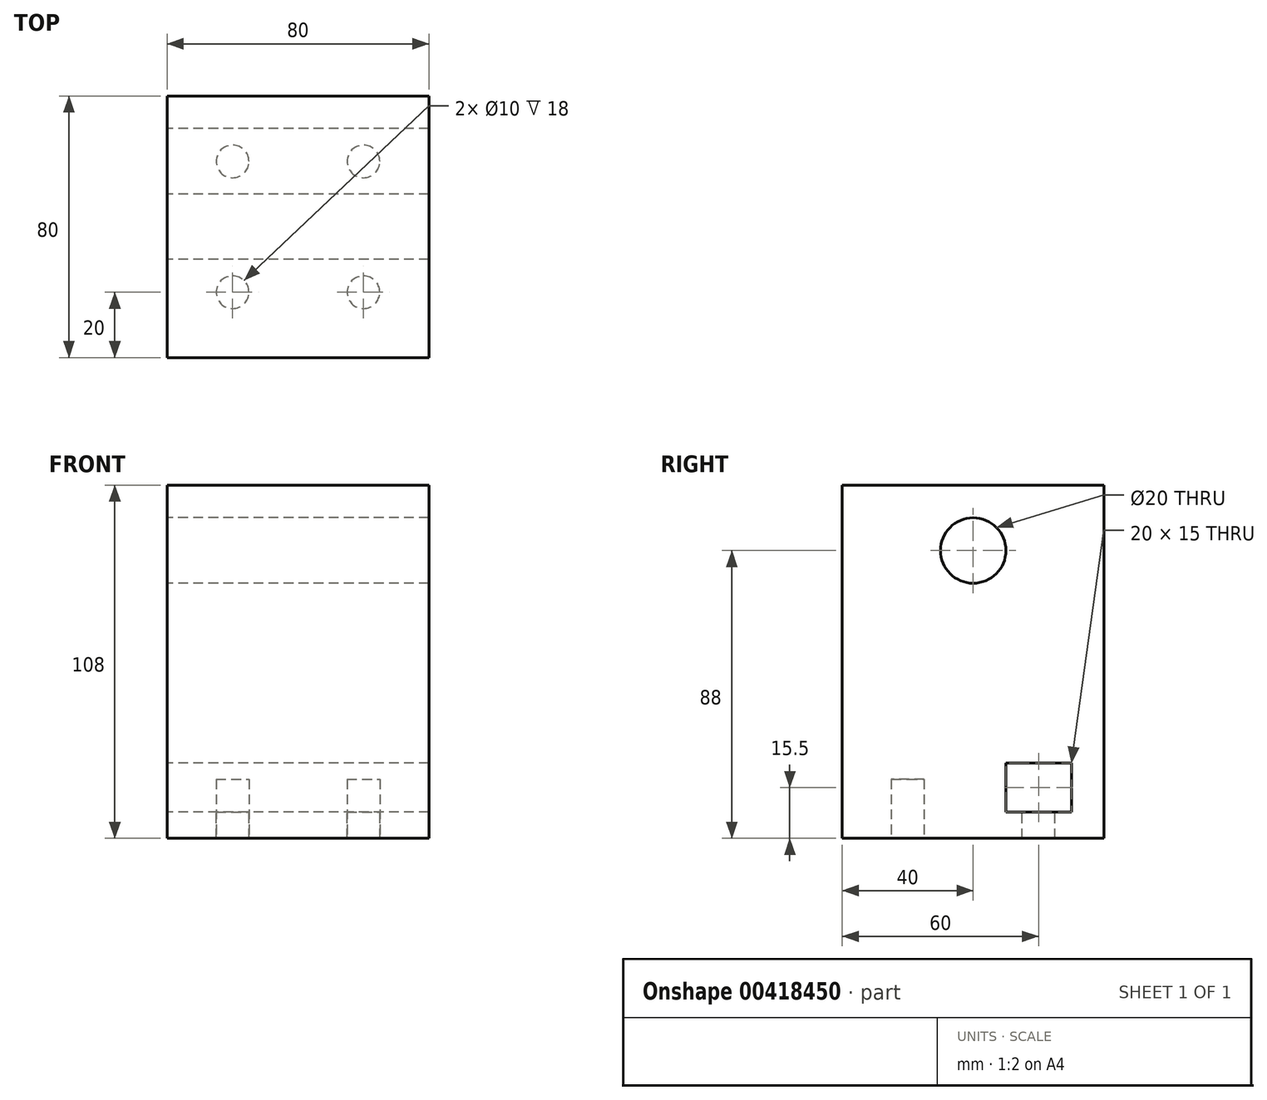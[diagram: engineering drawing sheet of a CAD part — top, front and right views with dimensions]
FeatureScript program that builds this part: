
annotation { "Feature Type Name" : "Feature", "Feature Type Description" : "" }
export const myFeature = defineFeature(function(context is Context, id is Id, definition is map)
    precondition{}
    {
        {
            var Q0;
            Q0=qCreatedBy(makeId("Top.planeOp"),FACE);
            var sketch = newSketch(context, id + "F0", { "sketchPlane" : qUnion([Q0])});
            skLineSegment(sketch, "E0.bottom", {"start": v(40, -40) * mm, "end": v(-40, -40) * mm});
            skLineSegment(sketch, "E0.top", {"start": v(40, 40) * mm, "end": v(-40, 40) * mm});
            skLineSegment(sketch, "E0.left", {"start": v(40, -40) * mm, "end": v(40, 40) * mm});
            skLineSegment(sketch, "E0.right", {"start": v(-40, -40) * mm, "end": v(-40, 40) * mm});
            skPoint(sketch, "E0.middle", {"position": v(0, 0) * mm});
            skSolve(sketch);
        }
        {
            var Q0;
            Q0=makeQuery(id+"F0.imprint","IMPRINT",FACE,{"disambiguationData":[TD([[makeQuery(id+"F0.imprint","IMPRINT",EDGE,{"derivedFrom":sQuery(id+"F0.wireOp",EDGE,"E0.bottom")}),-1.0]])]});
            extrude(context, id + "F1", {"entities" : qUnion([Q0]), "endBound" : BoundingType.SYMMETRIC, "depth" : 100 * mm});
        }
        {
            var Q0;
            Q0=makeQuery(id+"F1.opExtrude","CAP_FACE",FACE,{"disambiguationData":[OSD([sQuery(id+"F0.wireOp",EDGE,"E0.bottom"),sQuery(id+"F0.wireOp",EDGE,"E0.top"),sQuery(id+"F0.wireOp",EDGE,"E0.left"),sQuery(id+"F0.wireOp",EDGE,"E0.right")])],"isStart":true});
            var sketch = newSketch(context, id + "F2", { "sketchPlane" : qUnion([Q0])});
            skCircle(sketch, "E1", {"center": v(-20, 20) * mm, "radius": 5 * mm});
            skCircle(sketch, "E2.1.0", {"center": v(-20, -20) * mm, "radius": 5 * mm});
            skCircle(sketch, "E2.2.0", {"center": v(20, -20) * mm, "radius": 5 * mm});
            skCircle(sketch, "E2.3.0", {"center": v(20, 20) * mm, "radius": 5 * mm});
            skPoint(sketch, "E2.center", {"position": v(0, 0) * mm});
            skSolve(sketch);
        }
        {
            var Q0;
            Q0 = qSketchRegion(id + "F2", true);
            extrude(context, id + "F3", {"entities" : qUnion([Q0]), "operationType" : NewBodyOperationType.REMOVE, "oppositeDirection" : true, "depth" : 10 * mm});
        }
        {
            var Q0;
            Q0=makeQuery(id+"F1.opExtrude","SWEPT_FACE",FACE,{"disambiguationData":[OSD([sQuery(id+"F0.wireOp",EDGE,"E0.right")])]});
            var sketch = newSketch(context, id + "F4", { "sketchPlane" : qUnion([Q0])});
            skCircle(sketch, "E3", {"center": v(0, 30) * mm, "radius": 10 * mm});
            skSolve(sketch);
        }
        {
            var Q0;
            Q0=makeQuery(id+"F4.imprint","IMPRINT",FACE,{"disambiguationData":[TD([[makeQuery(id+"F4.imprint","IMPRINT",EDGE,{"derivedFrom":sQuery(id+"F4.wireOp",EDGE,"E3")}),1.0]])]});
            extrude(context, id + "F5", {"entities" : qUnion([Q0]), "operationType" : NewBodyOperationType.REMOVE, "oppositeDirection" : true, "depth" : 86.1 * mm});
        }
        {
            var Q0;
            Q0=makeQuery(id+"F1.opExtrude","SWEPT_FACE",FACE,{"disambiguationData":[OSD([sQuery(id+"F0.wireOp",EDGE,"E0.right")])]});
            var sketch = newSketch(context, id + "F6", { "sketchPlane" : qUnion([Q0])});
            skLineSegment(sketch, "E4.bottom", {"start": v(-30, -50) * mm, "end": v(-10, -50) * mm});
            skLineSegment(sketch, "E4.top", {"start": v(-30, -35) * mm, "end": v(-10, -35) * mm});
            skLineSegment(sketch, "E4.left", {"start": v(-30, -50) * mm, "end": v(-30, -35) * mm});
            skLineSegment(sketch, "E4.right", {"start": v(-10, -50) * mm, "end": v(-10, -35) * mm});
            skSolve(sketch);
        }
        {
            var Q0;
            Q0=makeQuery(id+"F6.imprint","IMPRINT",FACE,{"disambiguationData":[TD([[makeQuery(id+"F6.imprint","IMPRINT",EDGE,{"derivedFrom":sQuery(id+"F6.wireOp",EDGE,"E4.bottom")}),-1.0]])]});
            extrude(context, id + "F7", {"entities" : qUnion([Q0]), "operationType" : NewBodyOperationType.REMOVE, "oppositeDirection" : true, "depth" : 84.6 * mm});
        }
        {
            var Q0;
            Q0=makeQuery(id+"F2.imprint","IMPRINT",FACE,{"disambiguationData":[TD([[makeQuery(id+"F2.imprint","IMPRINT",EDGE,{"derivedFrom":sQuery(id+"F2.wireOp",EDGE,"E1")}),-1.0]])]});
            extrude(context, id + "F8", {"entities" : qUnion([Q0]), "operationType" : NewBodyOperationType.ADD, "depth" : 8 * mm});
        }
    });
